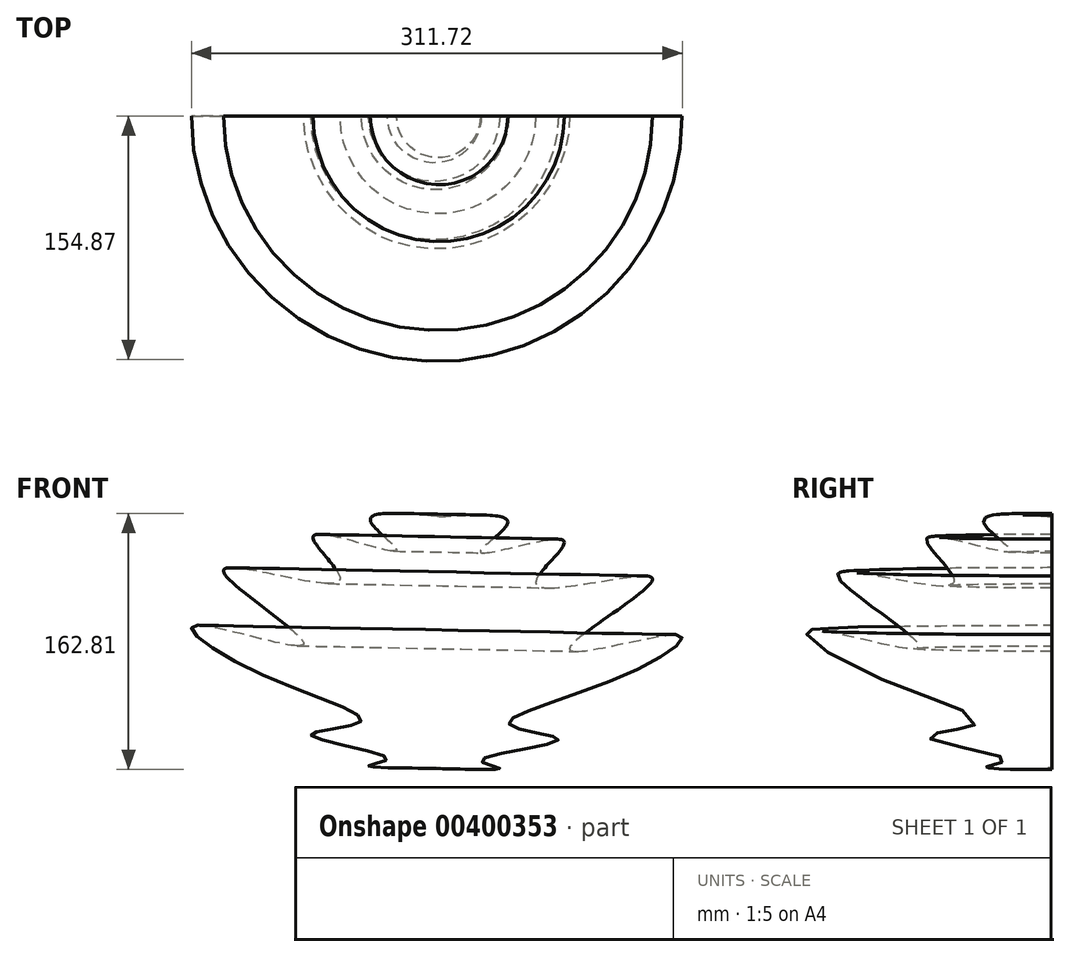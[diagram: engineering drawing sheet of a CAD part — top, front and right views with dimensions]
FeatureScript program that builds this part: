
annotation { "Feature Type Name" : "Feature", "Feature Type Description" : "" }
export const myFeature = defineFeature(function(context is Context, id is Id, definition is map)
    precondition{}
    {
        {
            var Q0;
            Q0=qCreatedBy(makeId("Front.planeOp"),FACE);
            var sketch = newSketch(context, id + "F0", { "sketchPlane" : qUnion([Q0])});
            skLineSegment(sketch, "E0", {"start": v(0, 75.13) * mm, "end": v(-3.17, -84.46) * mm});
            skFitSpline(sketch, "E1", {"points": [v(0, 75.13) * mm, v(43.36, 70.32) * mm, v(26.44, 52.4) * mm, v(79.31, 59.55) * mm, v(61.69, 31.9) * mm, v(135.36, 35.9) * mm, v(82.84, -8.87) * mm, v(151.92, 0) * mm, v(118.79, -25.28) * mm, v(45.12, -57.47) * mm, v(75.79, -66.6) * mm, v(26.79, -79.68) * mm, v(38.07, -84.54) * mm, v(-3.17, -84.46) * mm], "startDerivative": vector(926.77, 51.67) * mm, "endDerivative": vector(-926.5, 38.92) * mm});
            skSolve(sketch);
        }
        {
            var Q0;
            Q0=makeQuery(id+"F0.imprint","IMPRINT",FACE,{"disambiguationData":[TD([[makeQuery(id+"F0.imprint","IMPRINT",EDGE,{"derivedFrom":sQuery(id+"F0.wireOp",EDGE,"E0")}),1.0]])]});
            var Q1;
            Q1=sQuery(id+"F0.wireOp",EDGE,"E0");
            revolve(context, id + "F1", {"entities" : qUnion([Q0]), "axis" : qUnion([Q1]), "revolveType" : RevolveType.ONE_DIRECTION, "angle" : 180 * degree});
        }
    });
